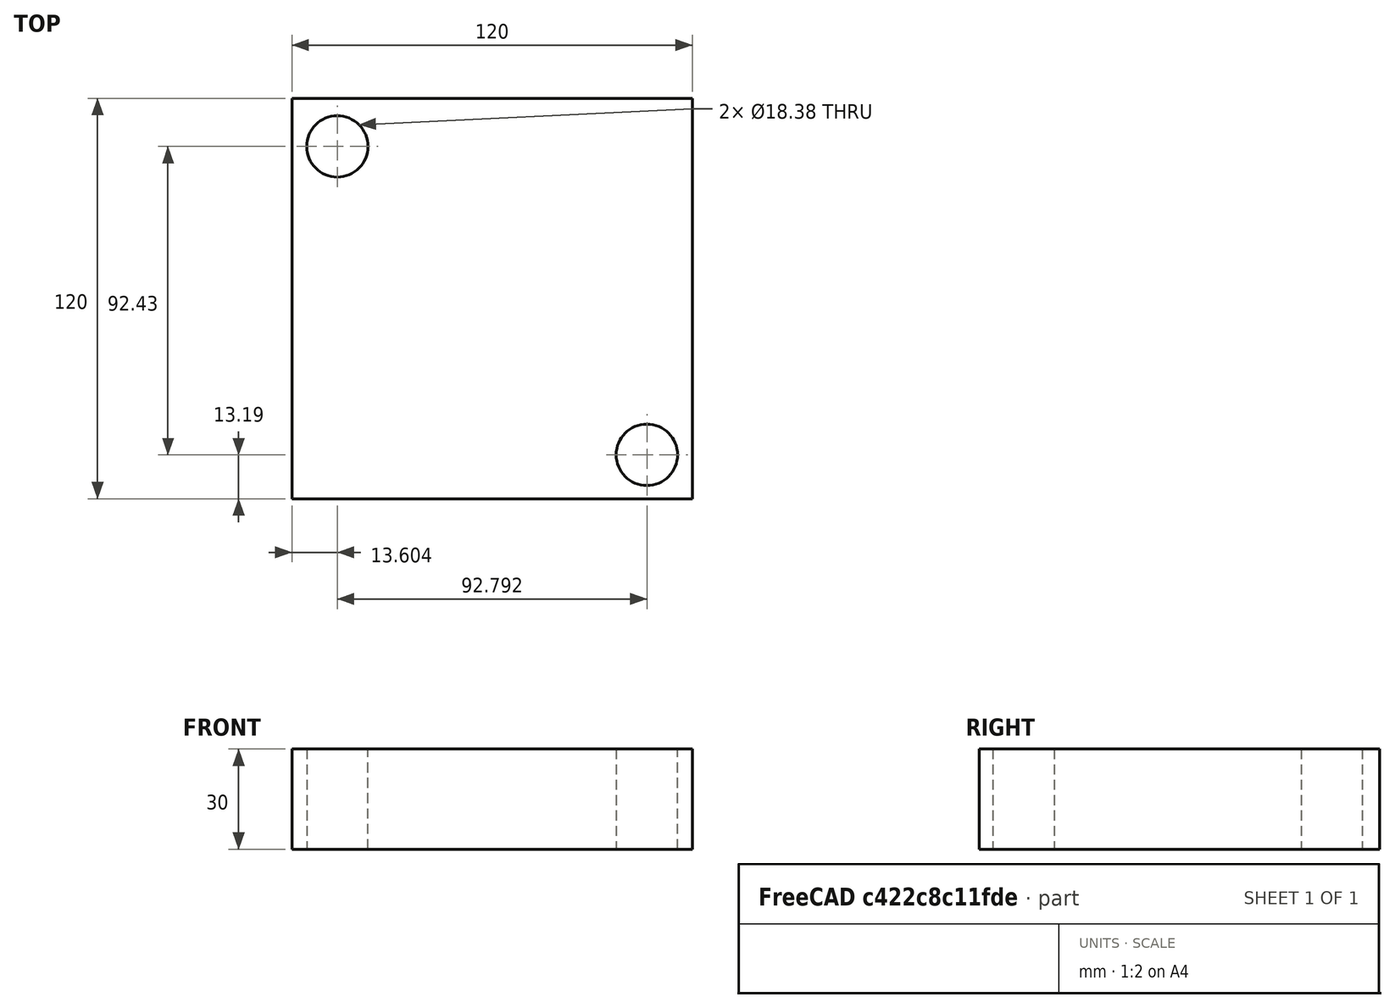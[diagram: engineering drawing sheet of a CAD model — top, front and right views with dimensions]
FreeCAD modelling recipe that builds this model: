
FCSTD DOCUMENT  (FreeCAD 0.18R16131 (Git))
Label: Momentum_Base
License: All rights reserved
LicenseURL: http://en.wikipedia.org/wiki/All_rights_reserved
objects: Sketcher::SketchObject×1, Part::Extrusion×1
note: 2 computed .brp shape members not serialized (recipe doc carries the construction recipe); baked Part::Feature solids carry a one-line shape summary decoded from their .brp

FEATURE [Sketcher::SketchObject] Sketch
  sketch-geometry (6):
    g0: LineSegment StartX=-66.9458 StartY=62.3125 StartZ=0 EndX=53.0542 EndY=62.3125 EndZ=0
    g1: LineSegment StartX=53.0542 StartY=62.3125 StartZ=0 EndX=53.0542 EndY=-57.6875 EndZ=0
    g2: LineSegment StartX=53.0542 StartY=-57.6875 StartZ=0 EndX=-66.9458 EndY=-57.6875 EndZ=0
    g3: LineSegment StartX=-66.9458 StartY=-57.6875 StartZ=0 EndX=-66.9458 EndY=62.3125 EndZ=0
    g4: Circle CenterX=-53.3461 CenterY=47.9303 CenterZ=0 NormalX=0 NormalY=0 NormalZ=1 AngleXU=0 Radius=9.191
    g5: Circle CenterX=39.4455 CenterY=-44.5002 CenterZ=0 NormalX=0 NormalY=0 NormalZ=1 AngleXU=0 Radius=9.191
  constraints (10):
    c: Coincident(g0,g1)
    c: Coincident(g1,g2)
    c: Coincident(g2,g3)
    c: Coincident(g3,g0)
    c: Horizontal(g0)
    c: Horizontal(g2)
    c: Vertical(g1)
    c: Vertical(g3)
    c: DistanceY(g3,g3) = 120
    c: DistanceX(g0,g0) = 120
FEATURE [Part::Extrusion] Extrude001
  Base = -> Sketch
  Dir = (0,0,1)
  DirMode = 2
  FaceMakerClass = Part::FaceMakerBullseye
  LengthFwd = 30
  LengthRev = 0
  Solid = true
  Symmetric = false
